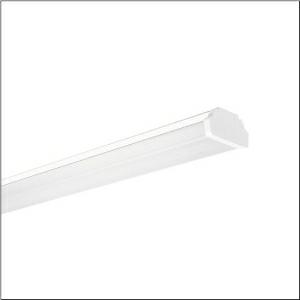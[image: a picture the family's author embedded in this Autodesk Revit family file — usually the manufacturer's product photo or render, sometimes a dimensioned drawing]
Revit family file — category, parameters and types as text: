
# Revit family: dus_31_gen_2_53bd812cv6c5d2_5d7c
name_source: partatom
category: Lighting Fixtures
units: mm (PartAtom-declared; Revit-internal decimal feet)

## family parameters
Cut with Voids When Loaded = No
Host = Face
Light Source = No
Part Type = Normal
Room Calculation Point = No
Round Connector Dimension = Use Diameter
Shared = No

## types (1)
- --- (1 x LED, 12660 lm, 68.5 W, 6500K)
    Apparent Load = 69 VA
    CIE Flux Codes = 47 80 95 93 100
    Color Rendering = 80
    Color Temperature = 6500K
    Default Elevation = 1800 mm
    Description = DUS 31 Gen.2, luminaire insert, of sheet steel, coil coated, white, length: 1.535mm, width: 81mm, height: 90mm, 5x system unit, system units: 307mm, LED rated luminous flux: 12.660lm, light colour: 865, SDCM (Standard Deviation of Colour Matching)MacAdam ≤ 3 SDCM (initial), control gear: ON/OFF Multilumen, CLOi, with plug, 3-pole, with phase selection, mains connection: 220..240V, AC, 50/60Hz, start of lifetime: 69W, end of service life: 82W, through-wiring accessed according to module size, primary optical cover: cover, of PMMA, light emission: direct distribution, primary light characteristic: symmetric, protection rating (complete): IP20, protection rating (LED compartment): IP50, insulation class (complete): insulation class I (protective earthing), certification: CE, ENEC, VDE, UKCA, impact resistance: IK03, permissible ambient temperature for indoor applications: -35..+35°C, corresponds to IFS (International Featured Standards) requirements for safety and quality in the food industry, reducing of maximum allowable ambient temperature of 5°C with ceiling mounting, packaging unit: 1 piece
    Height = 95 mm
    Lamp = 1 x LED
    Lamp Light Flux = 12660 lm
    Lamp Power = 68.5 W
    Lamp count = 1
    Length = 1535 mm
    Luminous efficacy = 185 lm/W
    Manufacturer = Siteco
    ModVariant = No
    Model = 53BD812CV6C5D2
    Mounting Place = Ceiling
    Mounting Type = Pendant
    Number of Poles = 1
    OnlyDefault = Yes
    Power Factor = 1
    Product Name = DUS 31 Gen.2
    Product group = luminaire insert | ceiling pendant
    ProductGroupID = 901
    Protection Class = Protection class I
    Protection Degree = IP 20
    RLX_Detail_Level = 1
    RLX_Emergency_Light_Flux = 0 lm
    RLX_Emergency_Type = 0
    RLX_Emergency_Type_DB = No
    RlxData = <blob elided: 29913 chars, md5=7baba28d>
    Socket = socket
    Standby Power = 0 W
    System Light Flux = 12660 lm
    System Power = 69 W
    Type Comments = factory setting: luminous flux: 100 % | (A | C | E) | 161 mA
    Type Image = l_1319596.jpg
    URL = http://relux.com
    VarID = @adj_049643
    Voltage = 0 V
    Weight = 0.00 kg
    Width = 81 mm

## geometry (parser evidence)
native form markers: Blend x4, Sweep x12
no freeform markers — native parametric forms only
